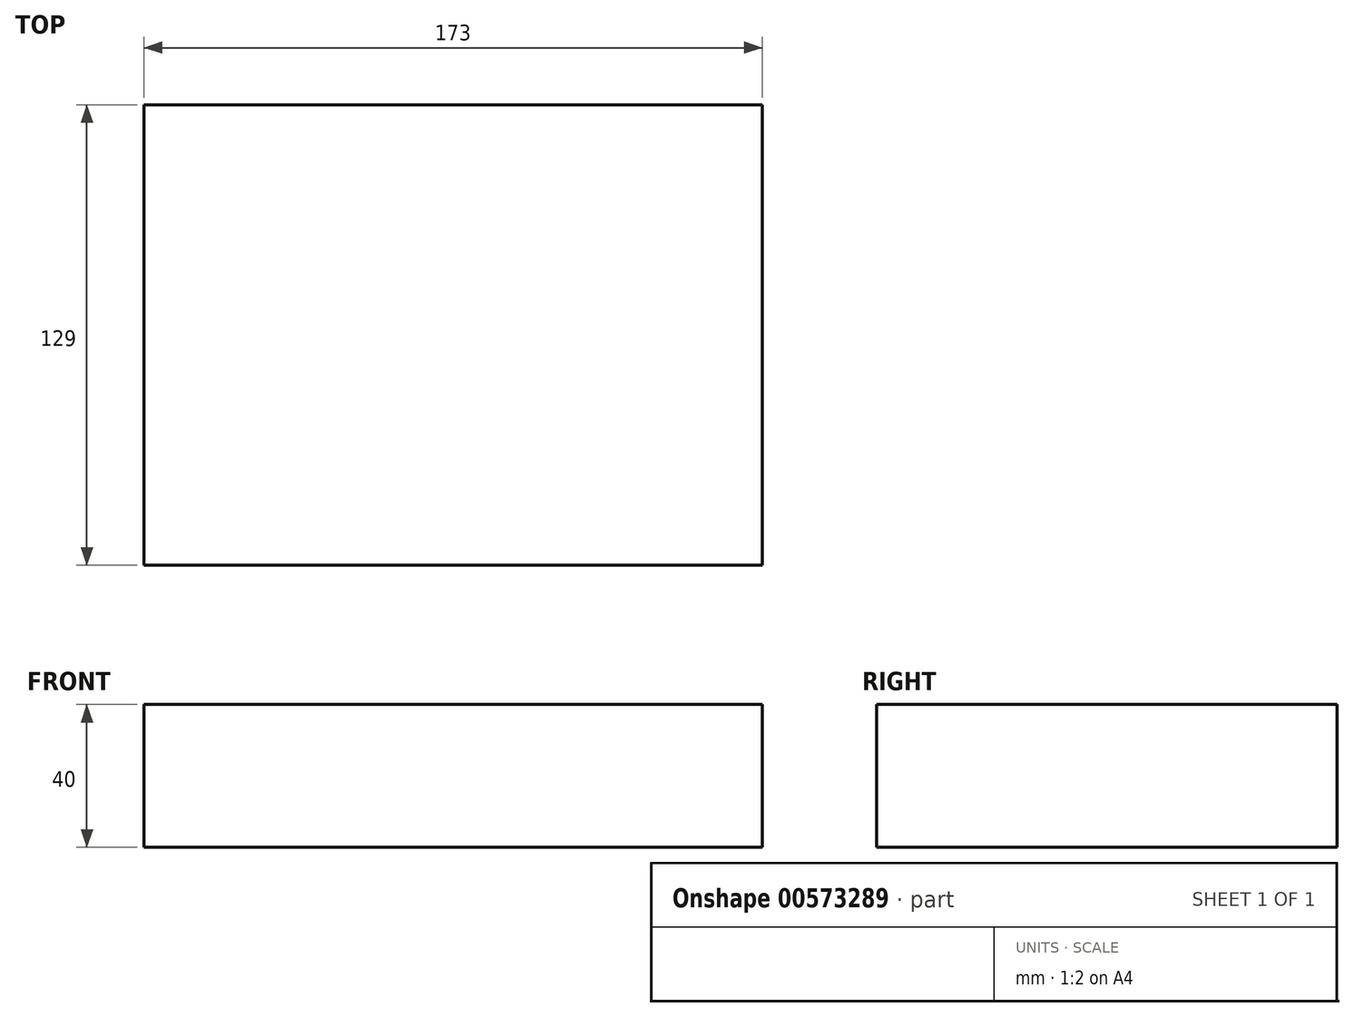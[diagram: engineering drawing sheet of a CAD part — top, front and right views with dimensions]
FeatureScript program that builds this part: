
annotation { "Feature Type Name" : "Feature", "Feature Type Description" : "" }
export const myFeature = defineFeature(function(context is Context, id is Id, definition is map)
    precondition{}
    {
        {
            var Q0;
            Q0=qCreatedBy(makeId("Top.planeOp"),FACE);
            var sketch = newSketch(context, id + "F0", { "sketchPlane" : qUnion([Q0])});
            skLineSegment(sketch, "E0.bottom", {"start": v(86.5, 64.5) * mm, "end": v(-86.5, 64.5) * mm});
            skLineSegment(sketch, "E0.top", {"start": v(86.5, -64.5) * mm, "end": v(-86.5, -64.5) * mm});
            skLineSegment(sketch, "E0.left", {"start": v(86.5, 64.5) * mm, "end": v(86.5, -64.5) * mm});
            skLineSegment(sketch, "E0.right", {"start": v(-86.5, 64.5) * mm, "end": v(-86.5, -64.5) * mm});
            skPoint(sketch, "E0.middle", {"position": v(0, 0) * mm});
            skSolve(sketch);
        }
        {
            var Q0;
            Q0=makeQuery(id+"F0.imprint","IMPRINT",FACE,{"disambiguationData":[TD([[makeQuery(id+"F0.imprint","IMPRINT",EDGE,{"derivedFrom":sQuery(id+"F0.wireOp",EDGE,"E0.bottom")}),1.0]])]});
            extrude(context, id + "F1", {"entities" : qUnion([Q0]), "depth" : 40 * mm, "offsetDistance" : 25 * mm});
        }
    });
